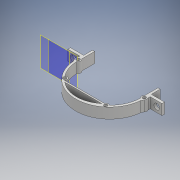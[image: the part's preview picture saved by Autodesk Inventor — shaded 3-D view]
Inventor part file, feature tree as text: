
AUTODESK INVENTOR PART (.ipt)
format: ipt  version: 2017 (Build 210142000, 142)  size: 231,936 bytes
history: native  units: mm
features: sketch x4, extrude x4, projected_geometry x4, other x2
ambient origin geometry x8: Origin, YZ Plane, XZ Plane, XY Plane, X Axis, Y Axis, Z Axis, Center Point
bodies: Body1 (feature_tree)
feature tree (14):
  sketch  "Esquisse1"
  other  "Plan de construction1"
  other  "Plan de construction2"
  sketch  "Esquisse3"
  extrude  "Extrusion16"  Depth=2.0mm
  extrude  "Extrusion17"  Depth=2.0mm
  extrude  "Extrusion18"  Depth=2.5mm
  extrude  "Extrusion19"  Depth=2.5mm
  projected_geometry  "Boucle projetée3"
  projected_geometry  "Boucle projetée4"
  sketch  "Esquisse5"
  projected_geometry  "Boucle projetée6"
  sketch  "Esquisse6"
  projected_geometry  "Boucle projetée7"
